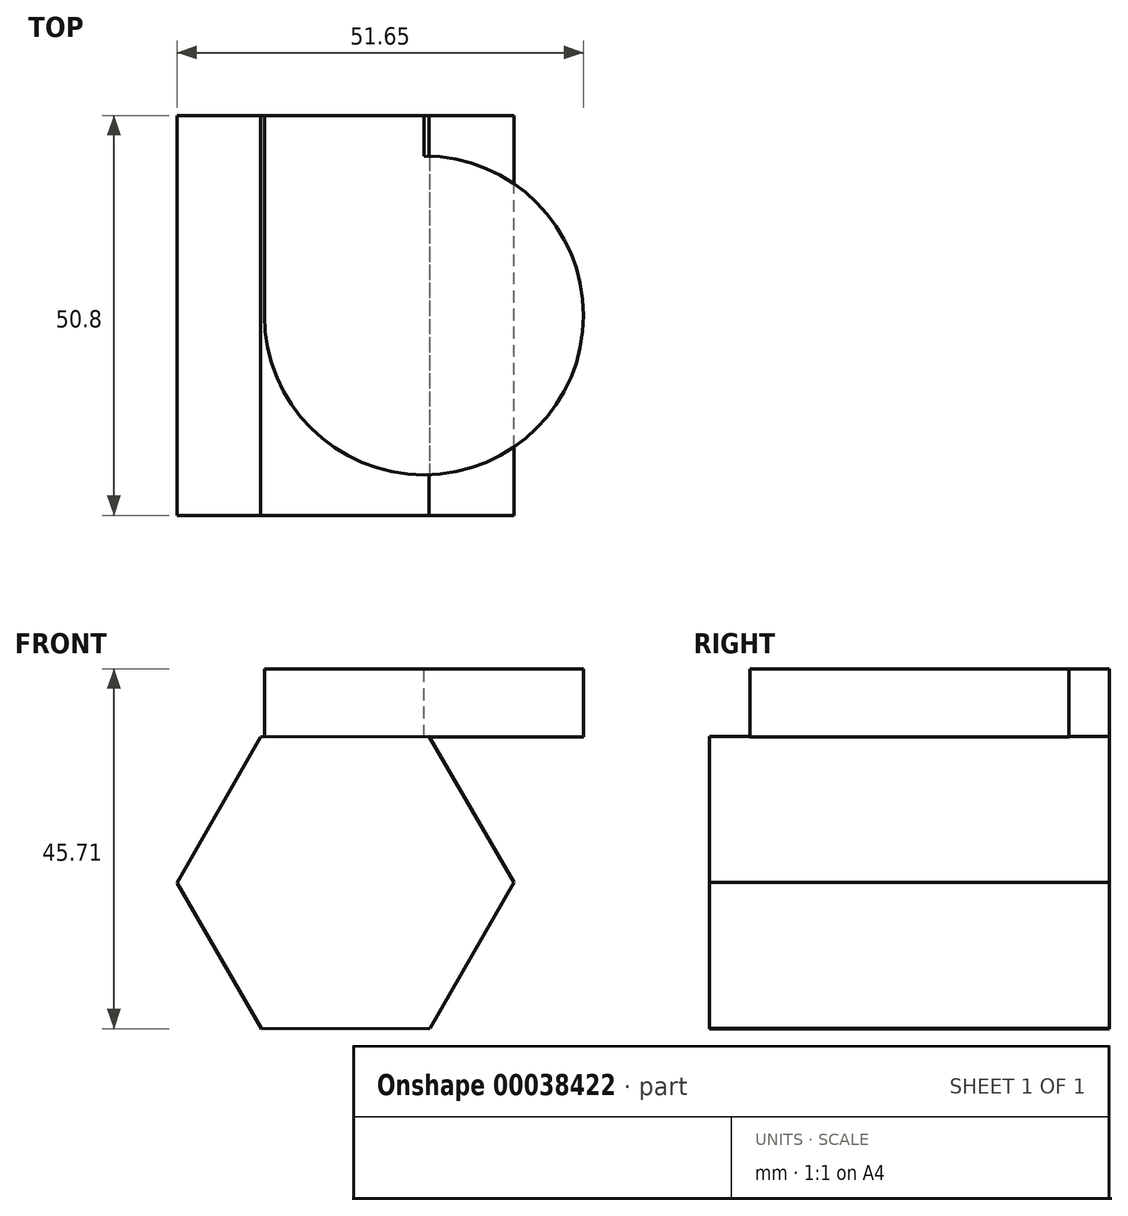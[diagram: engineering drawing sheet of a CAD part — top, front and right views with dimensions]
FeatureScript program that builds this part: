
annotation { "Feature Type Name" : "Feature", "Feature Type Description" : "" }
export const myFeature = defineFeature(function(context is Context, id is Id, definition is map)
    precondition{}
    {
        {
            var Q0;
            Q0=qCreatedBy(makeId("Front.planeOp"),FACE);
            var sketch = newSketch(context, id + "F0", { "sketchPlane" : qUnion([Q0])});
            skLineSegment(sketch, "E0", {"start": v(0, 6.35) * mm, "end": v(0, 49.76) * mm});
            skLineSegment(sketch, "E1", {"start": v(6.35, 56.11) * mm, "end": v(51.73, 56.11) * mm});
            skLineSegment(sketch, "E2", {"start": v(58.08, 49.76) * mm, "end": v(58.08, 6.35) * mm});
            skLineSegment(sketch, "E3", {"start": v(51.73, 0) * mm, "end": v(6.35, 0) * mm});
            skPoint(sketch, "E4.visualSharp", {"position": v(0, 56.11) * mm});
            skArc(sketch, "E4.filletArc", {"start": v(6.35, 56.11) * mm, "mid": v(1.86, 54.25) * mm, "end": v(0, 49.76) * mm});
            skPoint(sketch, "E5.visualSharp", {"position": v(58.08, 56.11) * mm});
            skArc(sketch, "E5.filletArc", {"start": v(58.08, 49.76) * mm, "mid": v(56.22, 54.25) * mm, "end": v(51.73, 56.11) * mm});
            skPoint(sketch, "E6.visualSharp", {"position": v(58.08, 0) * mm});
            skArc(sketch, "E6.filletArc", {"start": v(51.73, 0) * mm, "mid": v(56.22, 1.86) * mm, "end": v(58.08, 6.35) * mm});
            skPoint(sketch, "E7.visualSharp", {"position": v(0, 0) * mm});
            skArc(sketch, "E7.filletArc", {"start": v(0, 6.35) * mm, "mid": v(1.86, 1.86) * mm, "end": v(6.35, 0) * mm});
            skCircle(sketch, "E8.cCircle", {"center": v(29.04, 28.06) * mm, "radius": 18.54 * mm, "construction": true});
            skPoint(sketch, "E8.cCircle.centerSnap0", {"position": v(29.04, 56.11) * mm});
            skPoint(sketch, "E8.cCircle.centerSnap1", {"position": v(58.08, 28.06) * mm});
            skLineSegment(sketch, "E8.0", {"start": v(39.7, 46.61) * mm, "end": v(50.44, 28.1) * mm});
            skLineSegment(sketch, "E8.1", {"start": v(50.44, 28.1) * mm, "end": v(39.78, 9.54) * mm});
            skLineSegment(sketch, "E8.2", {"start": v(39.78, 9.54) * mm, "end": v(18.38, 9.5) * mm});
            skLineSegment(sketch, "E8.3", {"start": v(18.38, 9.5) * mm, "end": v(7.64, 28.01) * mm});
            skLineSegment(sketch, "E8.4", {"start": v(7.64, 28.01) * mm, "end": v(18.3, 46.57) * mm});
            skLineSegment(sketch, "E8.5", {"start": v(18.3, 46.57) * mm, "end": v(39.7, 46.61) * mm});
            skPoint(sketch, "E8.0.midPoint", {"position": v(45.07, 37.36) * mm});
            skLineSegment(sketch, "E9", {"start": v(0, 34.64) * mm, "end": v(-8.17, 34.64) * mm});
            skLineSegment(sketch, "E10", {"start": v(-8.17, 34.64) * mm, "end": v(-8.17, 24.65) * mm});
            skLineSegment(sketch, "E11", {"start": v(-8.17, 24.65) * mm, "end": v(0, 24.65) * mm});
            skSolve(sketch);
        }
        {
            var Q0;
            Q0=makeQuery(id+"F0.imprint","IMPRINT",FACE,{"disambiguationData":[TD([[makeQuery(id+"F0.imprint","IMPRINT",EDGE,{"derivedFrom":sQuery(id+"F0.wireOp",EDGE,"E8.0")}),-1.0]])]});
            extrude(context, id + "F1", {"entities" : qUnion([Q0]), "depth" : 50.8 * mm});
        }
        {
            var Q0;
            Q0=qCreatedBy(makeId("Front.planeOp"),FACE);
            var sketch = newSketch(context, id + "F2", { "sketchPlane" : qUnion([Q0])});
            skLineSegment(sketch, "E12.bottom", {"start": v(18.75, 46.43) * mm, "end": v(39.02, 46.43) * mm});
            skLineSegment(sketch, "E12.top", {"start": v(18.75, 55.2) * mm, "end": v(39.02, 55.2) * mm});
            skLineSegment(sketch, "E12.left", {"start": v(18.75, 46.43) * mm, "end": v(18.75, 55.2) * mm});
            skLineSegment(sketch, "E12.right", {"start": v(39.02, 46.43) * mm, "end": v(39.02, 55.2) * mm});
            skSolve(sketch);
        }
        {
            var Q0;
            Q0 = qSketchRegion(id + "F2", true);
            extrude(context, id + "F3", {"entities" : qUnion([Q0]), "operationType" : NewBodyOperationType.ADD, "depth" : 25.4 * mm});
        }
        {
            var Q0;
            Q0=makeQuery(id+"F3.opExtrude","CAP_FACE",FACE,{"disambiguationData":[OSD([sQuery(id+"F2.wireOp",EDGE,"E12.bottom"),sQuery(id+"F2.wireOp",EDGE,"E12.top"),sQuery(id+"F2.wireOp",EDGE,"E12.left"),sQuery(id+"F2.wireOp",EDGE,"E12.right")])],"isStart":false});
            var Q1;
            Q1=makeQuery(id+"F3.opExtrude","CAP_EDGE",EDGE,{"disambiguationData":[OSD([sQuery(id+"F2.wireOp",EDGE,"E12.right")])],"isStart":false});
            revolve(context, id + "F4", {"operationType" : NewBodyOperationType.ADD, "entities" : qUnion([Q0]), "axis" : qUnion([Q1]), "revolveType" : RevolveType.FULL});
        }
    });
